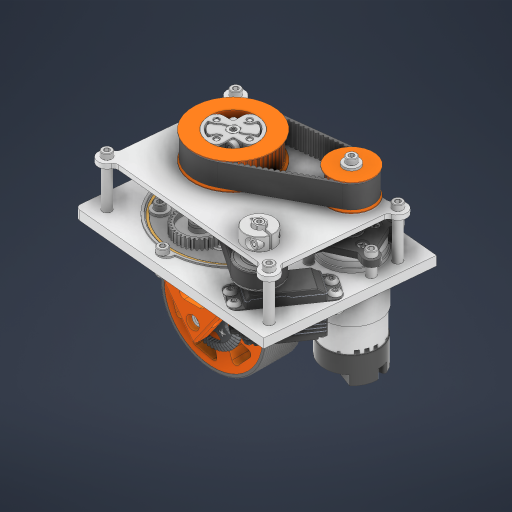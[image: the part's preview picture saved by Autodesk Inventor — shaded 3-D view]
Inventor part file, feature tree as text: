
AUTODESK INVENTOR PART (.ipt)
format: ipt  version: 2024.2 (Build 282272000, 272)  size: 59,912,192 bytes
history: native  units: in
note: dims shown in document units (in); Inventor stores cm internally (conversion verified against a paired STEP export)
features: other x130, plane x1
ambient origin geometry x8: Origin, YZ Plane, XZ Plane, XY Plane, X Axis, Y Axis, Z Axis, Center Point
bodies: Solid1 (feature_tree)
feature tree (131):
  other  "Pod.iam"
  other  "3ID3.5OD_Bearing.iam:1::outer race.ipt:1"
  other  "3ID3.5OD_Bearing.iam:1::shield.ipt:1"
  other  "3ID3.5OD_Bearing.iam:1::inner race.ipt:1"
  other  "AXON-ROBOTICS_PINION_BEVEL.ipt:1"
  other  "Modified_20Tooth_Pinion.ipt:1"
  other  "2807 Series Stainless Steel Shim (8mm ID x 11mm OD, 0.25mm Thickness) - 12 Pack.ipt:2"
  other  "Modified_36Tooth_Pinion.ipt:3"
  other  "AXON-ROBOTICS_HUB_BEVEL.ipt:1"
  other  "2801 Series Zinc-Plated Steel Washer (4mm ID x 11mm OD).ipt:1"
  other  "2802 Series Zinc-Plated Steel Button Head Screw (M4 x 0.7mm, 10mm Length) - 25 Pack.ipt:1"
  other  "Wheel_Base.ipt:1"
  other  "GGT.ipt:1"
  other  "2802 Series Zinc-Plated Steel Button Head Screw (M4 x 0.7mm, 10mm Length) - 25 Pack.ipt:2"
  other  "2801 Series Zinc Plated Steel Washer (4mm ID x 8mm OD) - 25 Pack.ipt:1"
  other  "1504 Series 32mm OD Pattern Spacer (2mm Length).ipt:1"
  other  "2807 Series Stainless Steel Shim (8mm ID x 11mm OD, 0.25mm Thickness) - 12 Pack.ipt:3"
  other  "2807 Series Stainless Steel Shim (8mm ID x 11mm OD, 0.25mm Thickness) - 12 Pack.ipt:4"
  other  "Rotation_Pulley.ipt:1"
  other  "1501 Series M4 x 0.7mm Standoff (6mm OD, 8mm Length) - 4 Pack.ipt:1"
  other  "1501 Series M4 x 0.7mm Standoff (6mm OD, 8mm Length) - 4 Pack.ipt:2"
  other  "1501 Series M4 x 0.7mm Standoff (6mm OD, 8mm Length) - 4 Pack.ipt:3"
  other  "1501 Series M4 x 0.7mm Standoff (6mm OD, 8mm Length) - 4 Pack.ipt:4"
  other  "Inner_Pod_Holder.ipt:1"
  other  "2801 Series Zinc-Plated Steel Washer (4mm ID x 11mm OD).ipt:2"
  other  "2801 Series Zinc-Plated Steel Washer (4mm ID x 11mm OD).ipt:3"
  other  "2801 Series Zinc-Plated Steel Washer (4mm ID x 11mm OD).ipt:4"
  other  "2801 Series Zinc-Plated Steel Washer (4mm ID x 11mm OD).ipt:5"
  other  "2801 Series Zinc-Plated Steel Washer (4mm ID x 11mm OD).ipt:6"
  other  "2801 Series Zinc-Plated Steel Washer (4mm ID x 11mm OD).ipt:7"
  other  "2801 Series Zinc-Plated Steel Washer (4mm ID x 11mm OD).ipt:8"
  other  "2801 Series Zinc-Plated Steel Washer (4mm ID x 11mm OD).ipt:9"
  other  "2800 Series Zinc-Plated Steel Socket Head Screw (M4 x 0.7mm, 14mm Length) - 25 Pack.ipt:1"
  other  "2800 Series Zinc-Plated Steel Socket Head Screw (M4 x 0.7mm, 14mm Length) - 25 Pack.ipt:2"
  other  "2800 Series Zinc-Plated Steel Socket Head Screw (M4 x 0.7mm, 14mm Length) - 25 Pack.ipt:3"
  other  "2800 Series Zinc-Plated Steel Socket Head Screw (M4 x 0.7mm, 14mm Length) - 25 Pack.ipt:4"
  other  "2812 Series Zinc-Plated Steel Nylon-Insert Locknut (M4 x 0.7mm, 7mm Hex) - 25 Pack.ipt:1"
  other  "2812 Series Zinc-Plated Steel Nylon-Insert Locknut (M4 x 0.7mm, 7mm Hex) - 25 Pack.ipt:2"
  other  "2812 Series Zinc-Plated Steel Nylon-Insert Locknut (M4 x 0.7mm, 7mm Hex) - 25 Pack.ipt:3"
  other  "2812 Series Zinc-Plated Steel Nylon-Insert Locknut (M4 x 0.7mm, 7mm Hex) - 25 Pack.ipt:4"
  other  "big_funny_washer.ipt:1"
  other  "2802 Series Zinc-Plated Steel Button Head Screw (M4 x 0.7mm, 10mm Length) - 25 Pack.ipt:3"
  other  "2802 Series Zinc-Plated Steel Button Head Screw (M4 x 0.7mm, 10mm Length) - 25 Pack.ipt:4"
  other  "2802 Series Zinc-Plated Steel Button Head Screw (M4 x 0.7mm, 10mm Length) - 25 Pack.ipt:5"
  other  "2802 Series Zinc-Plated Steel Button Head Screw (M4 x 0.7mm, 10mm Length) - 25 Pack.ipt:6"
  other  "2106 Series Stainless Steel REX Shaft (8mm Diameter, 40mm Length).iam:1::2106-4008-0400.ipt:1"
  other  "Wheel_Axle_Holder.ipt:1"
  other  "2801 Series Zinc Plated Steel Washer (4mm ID x 8mm OD) - 25 Pack.ipt:2"
  other  "2800 Series Zinc-Plated Steel Socket Head Screw (M4 x 0.7mm, 14mm Length) - 25 Pack.ipt:5"
  other  "2811 Series Zinc-Plated Steel Hex Nut (M4 x 0.7mm, 7mm Hex) - 25 Pack.ipt:1"
  other  "2811 Series Zinc-Plated Steel Hex Nut (M4 x 0.7mm, 7mm Hex) - 25 Pack.ipt:2"
  other  "2800 Series Zinc-Plated Steel Socket Head Screw (M4 x 0.7mm, 30mm Length) - 25 Pack.ipt:1"
  other  "2800 Series Zinc-Plated Steel Socket Head Screw (M4 x 0.7mm, 30mm Length) - 25 Pack.ipt:2"
  other  "HTD Pulley - 53 Tooth.ipt:1"
  other  "2807 Series Stainless Steel Shim (8mm ID x 11mm OD, 0.25mm Thickness) - 12 Pack.ipt:6"
  other  "28_Tooth.ipt:1"
  other  "2801 Series Zinc-Plated Steel Washer (4mm ID x 11mm OD).ipt:10"
  other  "2800 Series Zinc-Plated Steel Socket Head Screw (M4 x 0.7mm, 14mm Length) - 25 Pack.ipt:6"
  other  "Part Studio 1 - [LS] HTD3 belt 84 teeth.ipt:1"
  other  "1501 Series M4 x 0.7mm Standoff (6mm OD, 8mm Length) - 4 Pack.ipt:5"
  other  "Part Studio 1 - [LS] HTD5 belt 43 teeth.ipt:1"
  other  "Axon_MINI.iam:1::DDJ-STDLOW2-M2H-CNC.ipt:1"
  other  "Axon_MINI.iam:1::DDJ-STDLOW2-B-CNC.ipt:1"
  other  "Axon_MINI.iam:1::DDJ-STDLOW-LUOSI_3.ipt:1"
  other  "Axon_MINI.iam:1::DDJ-STDLOW-ZHOUCHENG.ipt:1"
  other  "Axon_MINI.iam:1::DDJ-STDLOW-LUOSI.ipt:1"
  other  "Axon_MINI.iam:1::DDJ-XT-22-3P.ipt:1"
  other  "Axon_MINI.iam:1::DDJ-STDLOW-LUOSI_1.ipt:1"
  other  "Axon_MINI.iam:1::DDJ-STDLOW-LUOSI_2.ipt:1"
  other  "Axon_MINI.iam:1::DDJ-STDLOW-GEAR6.ipt:1"
  other  "Lower_Plate.ipt:1"
  other  "1501 Series M4 x 0.7mm Standoff (6mm OD, 8mm Length) - 4 Pack.ipt:6"
  other  "2812 Series Zinc-Plated Steel Nylon-Insert Locknut (M4 x 0.7mm, 7mm Hex) - 25 Pack.ipt:5"
  other  "2802 Series Zinc-Plated Steel Button Head Screw (M4 x 0.7mm, 10mm Length) - 25 Pack.ipt:7"
  other  "2812 Series Zinc-Plated Steel Nylon-Insert Locknut (M4 x 0.7mm, 7mm Hex) - 25 Pack.ipt:6"
  other  "2802 Series Zinc-Plated Steel Button Head Screw (M4 x 0.7mm, 10mm Length) - 25 Pack.ipt:8"
  other  "2812 Series Zinc-Plated Steel Nylon-Insert Locknut (M4 x 0.7mm, 7mm Hex) - 25 Pack.ipt:7"
  other  "2802 Series Zinc-Plated Steel Button Head Screw (M4 x 0.7mm, 10mm Length) - 25 Pack.ipt:9"
  other  "2812 Series Zinc-Plated Steel Nylon-Insert Locknut (M4 x 0.7mm, 7mm Hex) - 25 Pack.ipt:8"
  other  "2802 Series Zinc-Plated Steel Button Head Screw (M4 x 0.7mm, 10mm Length) - 25 Pack.ipt:10"
  other  "2812 Series Zinc-Plated Steel Nylon-Insert Locknut (M4 x 0.7mm, 7mm Hex) - 25 Pack.ipt:9"
  other  "2800 Series Zinc-Plated Steel Socket Head Screw (M4 x 0.7mm, 12mm Length) - 25 Pack.ipt:1"
  other  "2812 Series Zinc-Plated Steel Nylon-Insert Locknut (M4 x 0.7mm, 7mm Hex) - 25 Pack.ipt:10"
  other  "2800 Series Zinc-Plated Steel Socket Head Screw (M4 x 0.7mm, 12mm Length) - 25 Pack.ipt:2"
  other  "2812 Series Zinc-Plated Steel Nylon-Insert Locknut (M4 x 0.7mm, 7mm Hex) - 25 Pack.ipt:11"
  other  "2800 Series Zinc-Plated Steel Socket Head Screw (M4 x 0.7mm, 12mm Length) - 25 Pack.ipt:3"
  other  "big_funny_washer.ipt:2"
  other  "2812 Series Zinc-Plated Steel Nylon-Insert Locknut (M4 x 0.7mm, 7mm Hex) - 25 Pack.ipt:13"
  other  "2800 Series Zinc-Plated Steel Socket Head Screw (M4 x 0.7mm, 12mm Length) - 25 Pack.ipt:5"
  other  "1501 Series M4 x 0.7mm Standoff (6mm OD, 8mm Length) - 4 Pack.ipt:7"
  other  "1501 Series M4 x 0.7mm Standoff (6mm OD, 8mm Length) - 4 Pack.ipt:8"
  other  "2800 Series Zinc-Plated Steel Socket Head Screw (M4 x 0.7mm, 14mm Length) - 25 Pack.ipt:7"
  other  "2800 Series Zinc-Plated Steel Socket Head Screw (M4 x 0.7mm, 14mm Length) - 25 Pack.ipt:8"
  other  "2800 Series Zinc-Plated Steel Socket Head Screw (M4 x 0.7mm, 14mm Length) - 25 Pack.ipt:9"
  other  "2800 Series Zinc-Plated Steel Socket Head Screw (M4 x 0.7mm, 14mm Length) - 25 Pack.ipt:10"
  other  "2800 Series Zinc-Plated Steel Socket Head Screw (M4 x 0.7mm, 7mm Length) - 25 Pack.ipt:1"
  other  "2800 Series Zinc-Plated Steel Socket Head Screw (M4 x 0.7mm, 7mm Length) - 25 Pack.ipt:2"
  other  "2800 Series Zinc-Plated Steel Socket Head Screw (M4 x 0.7mm, 7mm Length) - 25 Pack.ipt:3"
  other  "2800 Series Zinc-Plated Steel Socket Head Screw (M4 x 0.7mm, 7mm Length) - 25 Pack.ipt:4"
  other  "2800 Series Zinc-Plated Steel Socket Head Screw (M4 x 0.7mm, 7mm Length) - 25 Pack.ipt:5"
  other  "2800 Series Zinc-Plated Steel Socket Head Screw (M4 x 0.7mm, 7mm Length) - 25 Pack.ipt:6"
  other  "2800 Series Zinc-Plated Steel Socket Head Screw (M4 x 0.7mm, 7mm Length) - 25 Pack.ipt:7"
  other  "2800 Series Zinc-Plated Steel Socket Head Screw (M4 x 0.7mm, 7mm Length) - 25 Pack.ipt:8"
  other  "91698A729_Black-Oxide 18-8 Stainless Steel Phillips Flat Head Screws.ipt:1"
  other  "91698A729_Black-Oxide 18-8 Stainless Steel Phillips Flat Head Screws.ipt:2"
  other  "91698A729_Black-Oxide 18-8 Stainless Steel Phillips Flat Head Screws.ipt:3"
  other  "91698A729_Black-Oxide 18-8 Stainless Steel Phillips Flat Head Screws.ipt:4"
  other  "Wheel_Axle_Holder_MIR.ipt:1"
  other  "2800 Series Zinc-Plated Steel Socket Head Screw (M4 x 0.7mm, 14mm Length) - 25 Pack.ipt:11"
  other  "2811 Series Zinc-Plated Steel Hex Nut (M4 x 0.7mm, 7mm Hex) - 25 Pack.ipt:3"
  other  "2811 Series Zinc-Plated Steel Hex Nut (M4 x 0.7mm, 7mm Hex) - 25 Pack.ipt:4"
  other  "2800 Series Zinc-Plated Steel Socket Head Screw (M4 x 0.7mm, 30mm Length) - 25 Pack.ipt:3"
  other  "2800 Series Zinc-Plated Steel Socket Head Screw (M4 x 0.7mm, 30mm Length) - 25 Pack.ipt:4"
  other  "2807 Series Stainless Steel Shim (8mm ID x 11mm OD, 0.25mm Thickness) - 12 Pack.ipt:8"
  other  "Upper_Plate.ipt:1"
  other  "1501 Series M4 x 0.7mm Standoff (6mm OD, 28mm Length) - 4 Pack.ipt:1"
  other  "1501 Series M4 x 0.7mm Standoff (6mm OD, 28mm Length) - 4 Pack.ipt:2"
  other  "1501 Series M4 x 0.7mm Standoff (6mm OD, 28mm Length) - 4 Pack.ipt:3"
  other  "1501 Series M4 x 0.7mm Standoff (6mm OD, 28mm Length) - 4 Pack.ipt:4"
  other  "Power_Transmission_Spacer_One.ipt:1"
  other  "Servo_Spacer.ipt:1"
  other  "Power_Transmission_Space_Two.ipt:1"
  other  "2800 Series Zinc-Plated Steel Socket Head Screw (M4 x 0.7mm, 12mm Length) - 25 Pack.ipt:6"
  other  "2800 Series Zinc-Plated Steel Socket Head Screw (M4 x 0.7mm, 12mm Length) - 25 Pack.ipt:7"
  other  "2800 Series Zinc-Plated Steel Socket Head Screw (M4 x 0.7mm, 12mm Length) - 25 Pack.ipt:8"
  other  "2800 Series Zinc-Plated Steel Socket Head Screw (M4 x 0.7mm, 12mm Length) - 25 Pack.ipt:9"
  other  "2800 Series Zinc-Plated Steel Socket Head Screw (M4 x 0.7mm, 12mm Length) - 25 Pack.ipt:10"
  other  "2800 Series Zinc-Plated Steel Socket Head Screw (M4 x 0.7mm, 12mm Length) - 25 Pack.ipt:11"
  other  "2800 Series Zinc-Plated Steel Socket Head Screw (M4 x 0.7mm, 12mm Length) - 25 Pack.ipt:12"
  other  "2800 Series Zinc-Plated Steel Socket Head Screw (M4 x 0.7mm, 12mm Length) - 25 Pack.ipt:13"
  plane  "Work Plane2_1"
